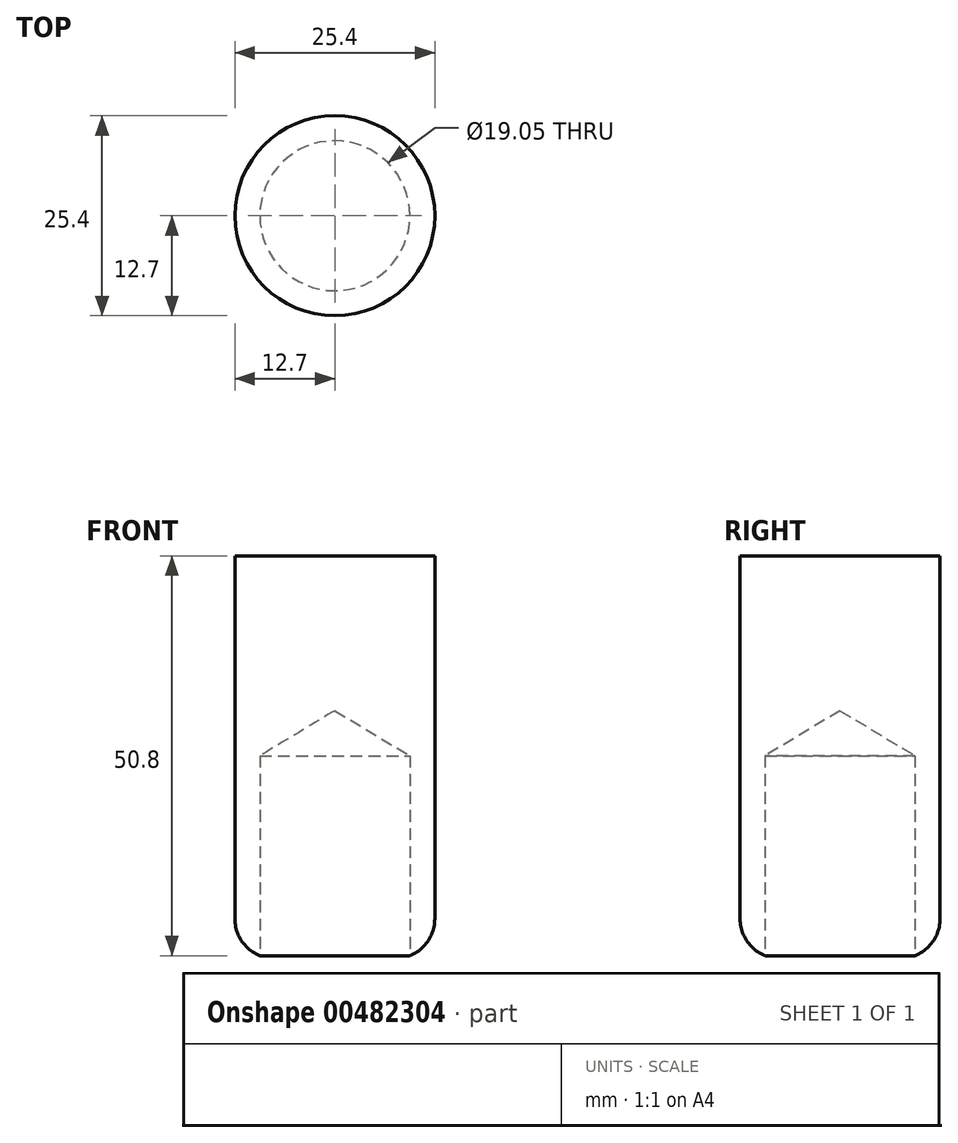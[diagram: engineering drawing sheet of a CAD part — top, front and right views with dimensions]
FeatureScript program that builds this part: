
annotation { "Feature Type Name" : "Feature", "Feature Type Description" : "" }
export const myFeature = defineFeature(function(context is Context, id is Id, definition is map)
    precondition{}
    {
        {
            var Q0;
            Q0=qCreatedBy(makeId("Top.planeOp"),FACE);
            var sketch = newSketch(context, id + "F0", { "sketchPlane" : qUnion([Q0])});
            skCircle(sketch, "E0", {"center": v(0, 0) * mm, "radius": 12.7 * mm});
            skSolve(sketch);
        }
        {
            var Q0;
            Q0 = qSketchRegion(id + "F0", true);
            extrude(context, id + "F1", {"entities" : qUnion([Q0]), "depth" : 50.8 * mm});
        }
        {
            var Q0;
            Q0=qCreatedBy(makeId("Top.planeOp"),FACE);
            var sketch = newSketch(context, id + "F2", { "sketchPlane" : qUnion([Q0])});
            skCircle(sketch, "E1", {"center": v(0, 0) * mm, "radius": 10.2 * mm});
            skSolve(sketch);
        }
        {
            var Q0;
            Q0=sQuery(id+"F2.wireOp",VERTEX,"E1.center");
            var Q1;
            Q1=makeQuery(id+"F1.opExtrude","SWEPT_BODY",BODY,{"disambiguationData":[OSD([sQuery(id+"F0.wireOp",EDGE,"E0")])]});
            hole(context, id + "F3", {"style" : HoleStyle.SIMPLE, "endStyle" : HoleEndStyle.BLIND, "oppositeDirection" : true, "holeDiameter" : 19.05 * mm, "holeDepth" : 25.4 * mm, "isTappedThrough" : true, "tappedDepth" : 12.7 * mm, "tapClearance" : 3, "locations" : qUnion([Q0]), "scope" : qUnion([Q1])});
        }
        {
            var Q0;
            Q0=makeQuery(id+"F1.opExtrude","CAP_EDGE",EDGE,{"disambiguationData":[OSD([sQuery(id+"F0.wireOp",EDGE,"E0")])],"isStart":true});
            fillet(context, id + "F4", {"entities" : qUnion([Q0]), "radius" : 5.08 * mm, "tangentPropagation" : true, "allowEdgeOverflow" : false});
        }
    });
